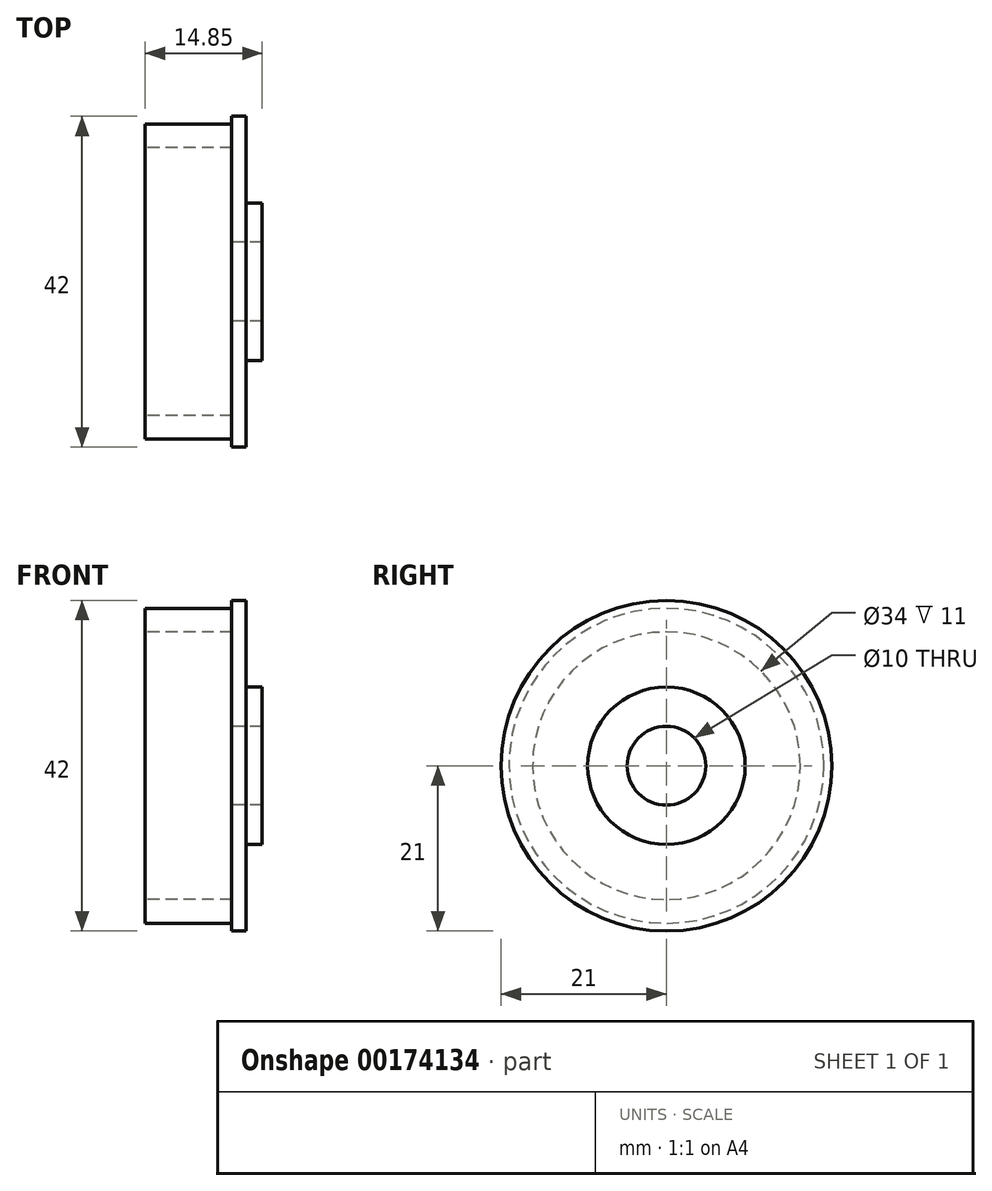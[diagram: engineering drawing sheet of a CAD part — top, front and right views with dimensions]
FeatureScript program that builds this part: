
annotation { "Feature Type Name" : "Feature", "Feature Type Description" : "" }
export const myFeature = defineFeature(function(context is Context, id is Id, definition is map)
    precondition{}
    {
        {
            var Q0;
            Q0=qCreatedBy(makeId("Front.planeOp"),FACE);
            var sketch = newSketch(context, id + "F0", { "sketchPlane" : qUnion([Q0])});
            skLineSegment(sketch, "E0", {"start": v(-48.86, 0) * mm, "end": v(57.65, 0) * mm});
            skLineSegment(sketch, "E1", {"start": v(0, 0) * mm, "end": v(0, 5) * mm});
            skLineSegment(sketch, "E2", {"start": v(0, 5) * mm, "end": v(0, 21) * mm});
            skLineSegment(sketch, "E3", {"start": v(0, 21) * mm, "end": v(1.85, 21) * mm});
            skLineSegment(sketch, "E4", {"start": v(1.85, 21) * mm, "end": v(1.85, 5) * mm});
            skLineSegment(sketch, "E5", {"start": v(1.85, 5) * mm, "end": v(0, 5) * mm});
            skLineSegment(sketch, "E6", {"start": v(0, 21) * mm, "end": v(0, 20) * mm});
            skLineSegment(sketch, "E7", {"start": v(0, 20) * mm, "end": v(-11, 20) * mm});
            skLineSegment(sketch, "E8", {"start": v(-11, 20) * mm, "end": v(-11, 17) * mm});
            skLineSegment(sketch, "E9", {"start": v(-11, 17) * mm, "end": v(0, 17) * mm});
            skLineSegment(sketch, "E10", {"start": v(1.85, 5) * mm, "end": v(3.85, 5) * mm});
            skLineSegment(sketch, "E11", {"start": v(3.85, 5) * mm, "end": v(3.85, 10) * mm});
            skLineSegment(sketch, "E12", {"start": v(3.85, 10) * mm, "end": v(1.85, 10) * mm});
            skSolve(sketch);
        }
        {
            var Q0;
            {var subQ0=sQuery(id+"F0.wireOp",EDGE,"E7");Q0=makeQuery(id+"F0.imprint","IMPRINT",FACE,{"disambiguationData":[TD([[makeQuery(id+"F0.imprint","IMPRINT",EDGE,{"derivedFrom":subQ0}),1.0]])]});}
            var Q1;
            {var subQ1=sQuery(id+"F0.wireOp",EDGE,"E3");Q1=makeQuery(id+"F0.imprint","IMPRINT",FACE,{"disambiguationData":[TD([[makeQuery(id+"F0.imprint","IMPRINT",EDGE,{"derivedFrom":subQ1}),-1.0]])]});}
            var Q2;
            {var subQ0=sQuery(id+"F0.wireOp",EDGE,"E10");Q2=makeQuery(id+"F0.imprint","IMPRINT",FACE,{"disambiguationData":[TD([[makeQuery(id+"F0.imprint","IMPRINT",EDGE,{"derivedFrom":subQ0}),1.0]])]});}
            var Q3;
            Q3=sQuery(id+"F0.wireOp",EDGE,"E0");
            revolve(context, id + "F1", {"entities" : qUnion([Q0, Q1, Q2]), "axis" : qUnion([Q3]), "revolveType" : RevolveType.FULL});
        }
    });
